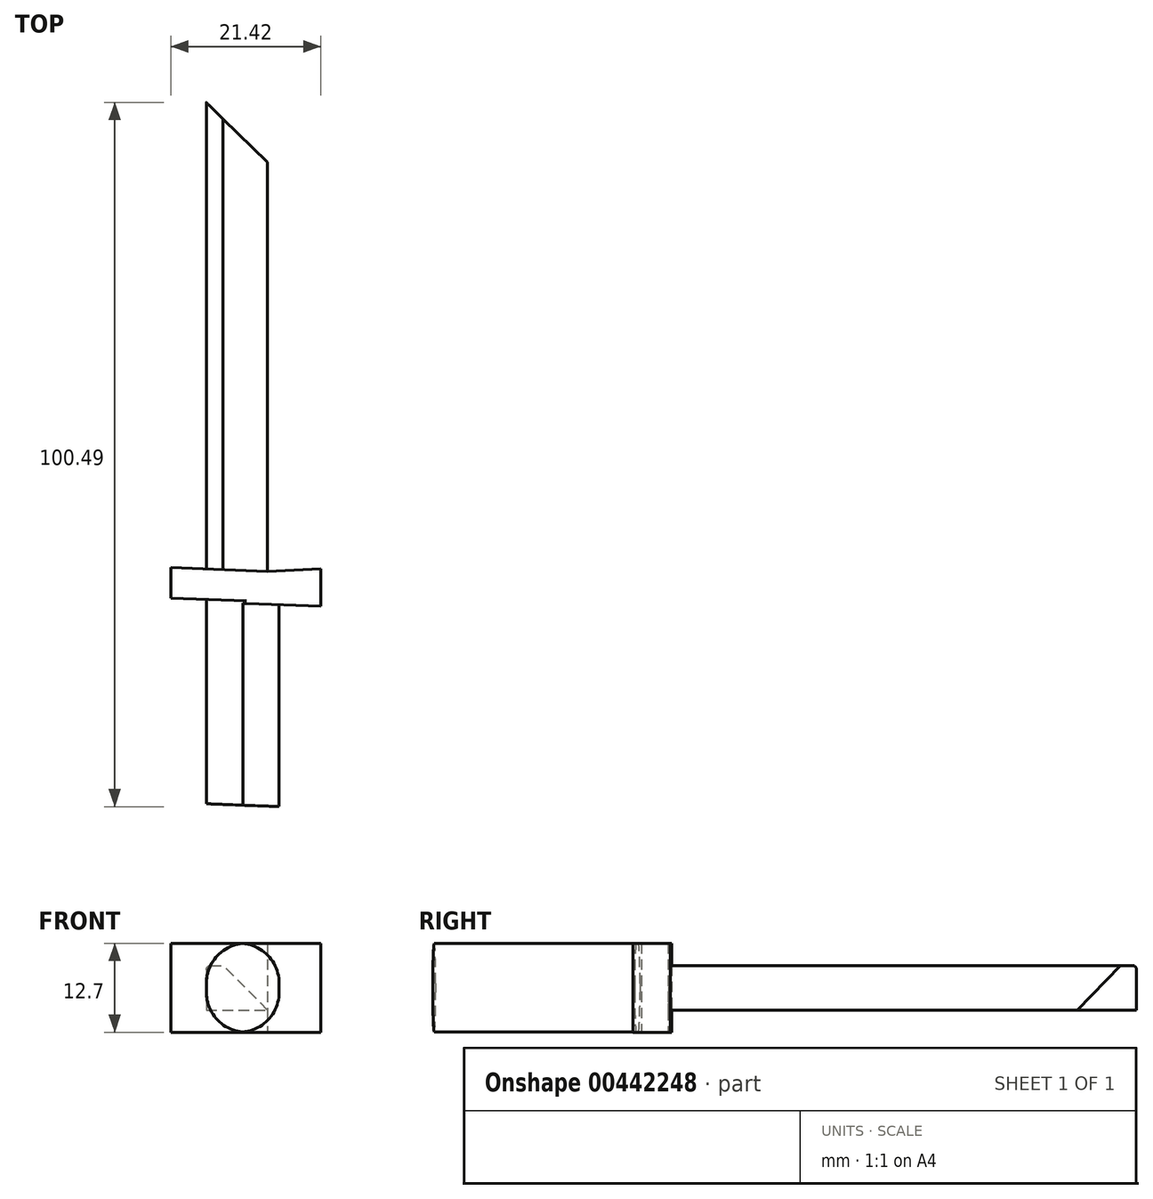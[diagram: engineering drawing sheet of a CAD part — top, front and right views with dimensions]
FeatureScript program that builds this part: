
annotation { "Feature Type Name" : "Feature", "Feature Type Description" : "" }
export const myFeature = defineFeature(function(context is Context, id is Id, definition is map)
    precondition{}
    {
        {
            var Q0;
            Q0=qCreatedBy(makeId("Top.planeOp"),FACE);
            var sketch = newSketch(context, id + "F0", { "sketchPlane" : qUnion([Q0])});
            skLineSegment(sketch, "E0", {"start": v(-41.67, -6.61) * mm, "end": v(-41.67, 59.96) * mm});
            skLineSegment(sketch, "E1", {"start": v(-41.67, 59.96) * mm, "end": v(-32.92, 51.47) * mm});
            skLineSegment(sketch, "E2", {"start": v(-32.92, 51.47) * mm, "end": v(-32.92, -6.95) * mm});
            skLineSegment(sketch, "E3", {"start": v(-32.92, -6.95) * mm, "end": v(-41.67, -6.61) * mm});
            skLineSegment(sketch, "E4", {"start": v(-41.67, -6.61) * mm, "end": v(-46.76, -6.41) * mm});
            skLineSegment(sketch, "E5", {"start": v(-46.76, -6.41) * mm, "end": v(-46.76, -10.75) * mm});
            skLineSegment(sketch, "E6", {"start": v(-46.76, -10.75) * mm, "end": v(-41.67, -10.94) * mm});
            skLineSegment(sketch, "E7", {"start": v(-41.67, -10.94) * mm, "end": v(-41.67, -40.12) * mm});
            skLineSegment(sketch, "E8", {"start": v(-41.67, -40.12) * mm, "end": v(-31.28, -40.53) * mm});
            skLineSegment(sketch, "E9", {"start": v(-31.28, -40.53) * mm, "end": v(-31.28, -11.7) * mm});
            skLineSegment(sketch, "E10", {"start": v(-31.28, -11.7) * mm, "end": v(-25.34, -11.93) * mm});
            skLineSegment(sketch, "E11", {"start": v(-25.34, -11.93) * mm, "end": v(-25.34, -6.61) * mm});
            skLineSegment(sketch, "E12", {"start": v(-32.92, -6.95) * mm, "end": v(-25.34, -6.61) * mm});
            skSolve(sketch);
        }
        {
            var Q0;
            Q0=makeQuery(id+"F0.imprint","IMPRINT",FACE,{"disambiguationData":[TD([[makeQuery(id+"F0.imprint","IMPRINT",EDGE,{"derivedFrom":sQuery(id+"F0.wireOp",EDGE,"E0")}),-1.0]])]});
            extrude(context, id + "F1", {"entities" : qUnion([Q0]), "depth" : 3.17 * mm, "hasSecondDirection" : true, "secondDirectionOppositeDirection" : true, "secondDirectionDepth" : 3.17 * mm});
        }
        {
            var Q0;
            Q0=makeQuery(id+"F0.imprint","IMPRINT",FACE,{"disambiguationData":[TD([[makeQuery(id+"F0.imprint","IMPRINT",EDGE,{"derivedFrom":sQuery(id+"F0.wireOp",EDGE,"E3")}),1.0]])]});
            extrude(context, id + "F2", {"entities" : qUnion([Q0]), "operationType" : NewBodyOperationType.ADD, "depth" : 6.35 * mm, "hasSecondDirection" : true, "secondDirectionOppositeDirection" : true, "secondDirectionDepth" : 6.35 * mm});
        }
        {
            var Q0;
            Q0=makeQuery(id+"F1.opExtrude","CAP_EDGE",EDGE,{"disambiguationData":[OSD([sQuery(id+"F0.wireOp",EDGE,"E2")])],"isStart":false});
            chamfer(context, id + "F3", {"entities" : qUnion([Q0]), "width" : 6.35 * mm, "tangentPropagation" : true});
        }
        {
            var Q0;
            Q0=makeQuery(id+"F2.opExtrude","CAP_EDGE",EDGE,{"disambiguationData":[OSD([sQuery(id+"F0.wireOp",EDGE,"E9")])],"isStart":false});
            var Q1;
            Q1=makeQuery(id+"F2.opExtrude","CAP_EDGE",EDGE,{"disambiguationData":[OSD([sQuery(id+"F0.wireOp",EDGE,"E7")])],"isStart":false});
            var Q2;
            Q2=makeQuery(id+"F2.opExtrude","CAP_EDGE",EDGE,{"disambiguationData":[OSD([sQuery(id+"F0.wireOp",EDGE,"E9")])],"isStart":true});
            var Q3;
            Q3=makeQuery(id+"F2.opExtrude","CAP_EDGE",EDGE,{"disambiguationData":[OSD([sQuery(id+"F0.wireOp",EDGE,"E7")])],"isStart":true});
            fillet(context, id + "F4", {"entities" : qUnion([Q0, Q1, Q2, Q3]), "radius" : 5.7 * mm, "tangentPropagation" : true, "allowEdgeOverflow" : false});
        }
        {
            var Q0;
            Q0=makeQuery(id+"F1.opExtrude","CAP_EDGE",EDGE,{"disambiguationData":[OSD([sQuery(id+"F0.wireOp",EDGE,"E0")])],"isStart":false});
            fillet(context, id + "F5", {"entities" : qUnion([Q0]), "radius" : 0.64 * mm, "tangentPropagation" : true, "allowEdgeOverflow" : false});
        }
    });
